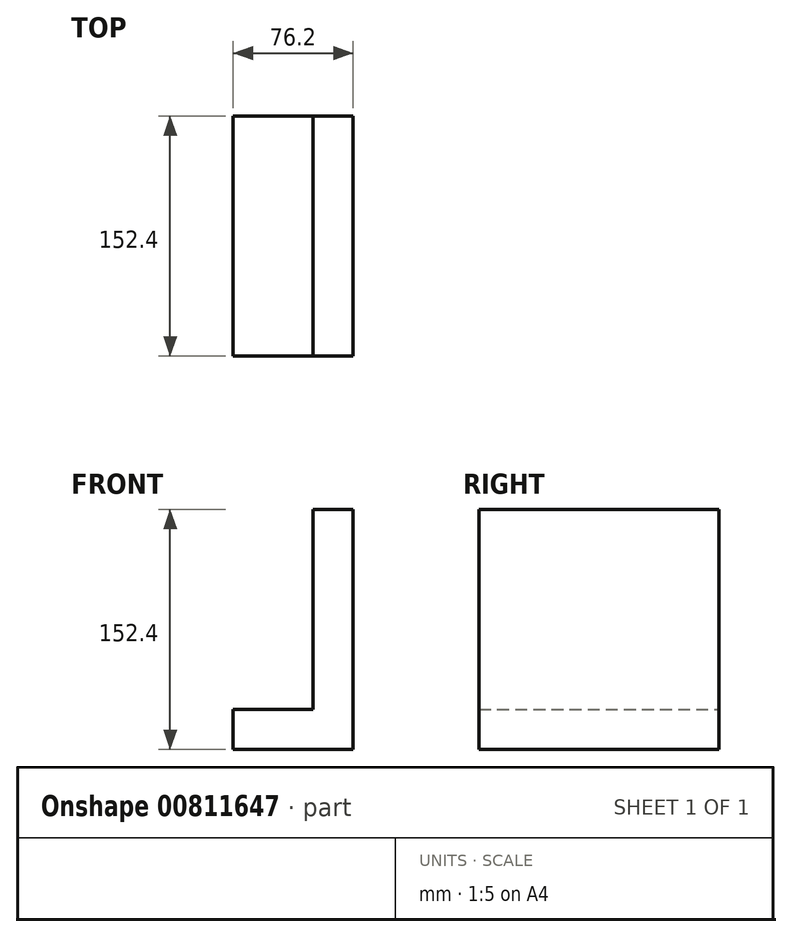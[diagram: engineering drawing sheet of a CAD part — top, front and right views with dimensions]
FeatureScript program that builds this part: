
annotation { "Feature Type Name" : "Feature", "Feature Type Description" : "" }
export const myFeature = defineFeature(function(context is Context, id is Id, definition is map)
    precondition{}
    {
        {
            var Q0;
            Q0=qCreatedBy(makeId("Front.planeOp"),FACE);
            var sketch = newSketch(context, id + "F0", { "sketchPlane" : qUnion([Q0])});
            skLineSegment(sketch, "E0", {"start": v(0, 0) * mm, "end": v(0, 152.4) * mm});
            skLineSegment(sketch, "E1", {"start": v(0, 152.4) * mm, "end": v(-25.4, 152.4) * mm});
            skLineSegment(sketch, "E2", {"start": v(-25.4, 152.4) * mm, "end": v(-25.4, 25.4) * mm});
            skLineSegment(sketch, "E3", {"start": v(-25.4, 25.4) * mm, "end": v(-76.2, 25.4) * mm});
            skLineSegment(sketch, "E4", {"start": v(-76.2, 25.4) * mm, "end": v(-76.2, 0) * mm});
            skLineSegment(sketch, "E5", {"start": v(-76.2, 0) * mm, "end": v(0, 0) * mm});
            skSolve(sketch);
        }
        {
            var Q0;
            Q0 = qSketchRegion(id + "F0", true);
            extrude(context, id + "F1", {"entities" : qUnion([Q0]), "endBound" : BoundingType.SYMMETRIC, "depth" : 152.4 * mm, "offsetDistance" : 25.4 * mm});
        }
    });
